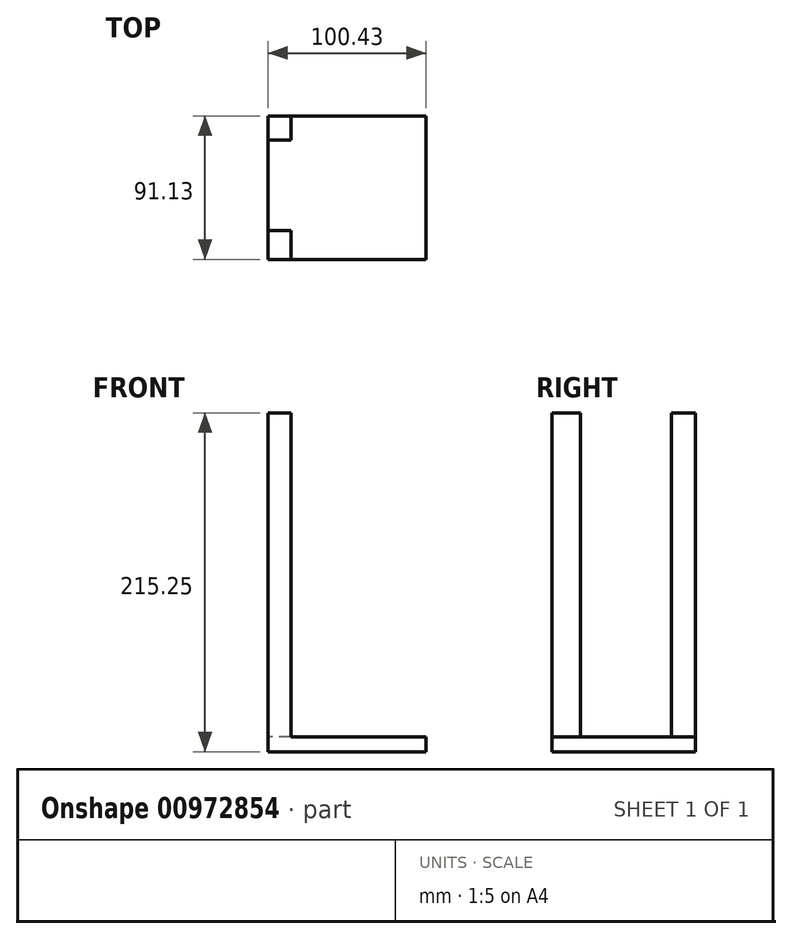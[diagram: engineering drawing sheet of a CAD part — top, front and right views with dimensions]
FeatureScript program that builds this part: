
annotation { "Feature Type Name" : "Feature", "Feature Type Description" : "" }
export const myFeature = defineFeature(function(context is Context, id is Id, definition is map)
    precondition{}
    {
        {
            var Q0;
            Q0=qCreatedBy(makeId("Top.planeOp"),FACE);
            var sketch = newSketch(context, id + "F0", { "sketchPlane" : qUnion([Q0])});
            skLineSegment(sketch, "E0.bottom", {"start": v(-43.08, 37.12) * mm, "end": v(57.35, 37.12) * mm});
            skLineSegment(sketch, "E0.top", {"start": v(-43.08, -54.01) * mm, "end": v(57.35, -54.01) * mm});
            skLineSegment(sketch, "E0.left", {"start": v(-43.08, 37.12) * mm, "end": v(-43.08, -54.01) * mm});
            skLineSegment(sketch, "E0.right", {"start": v(57.35, 37.12) * mm, "end": v(57.35, -54.01) * mm});
            skLineSegment(sketch, "E1", {"start": v(-29.36, 37.12) * mm, "end": v(-29.36, -54.01) * mm});
            skLineSegment(sketch, "E2", {"start": v(40.88, 37.12) * mm, "end": v(40.88, -54.01) * mm});
            skLineSegment(sketch, "E3", {"start": v(-43.08, 23.98) * mm, "end": v(57.35, 23.98) * mm});
            skLineSegment(sketch, "E4", {"start": v(-43.08, -38.08) * mm, "end": v(57.35, -38.08) * mm});
            skSolve(sketch);
        }
        {
            var Q0;
            {var subQ0=sQuery(id+"F0.wireOp",EDGE,"E0.right");var subQ1=sQuery(id+"F0.wireOp",EDGE,"E0.bottom");var subQ2=makeQuery(id+"F0.imprint","INTERSECT",VERTEX,{"derivedFrom":[subQ1,subQ0]});Q0=makeQuery(id+"F0.imprint","IMPRINT",FACE,{"disambiguationData":[TD([[makeQuery(id+"F0.imprint","IMPRINT",EDGE,{"disambiguationData":[TD([[subQ2,1.0]])],"derivedFrom":subQ1}),-1.0]])]});}
            var Q1;
            {var subQ0=sQuery(id+"F0.wireOp",EDGE,"E3");var subQ1=sQuery(id+"F0.wireOp",EDGE,"E0.right");var subQ2=makeQuery(id+"F0.imprint","INTERSECT",VERTEX,{"derivedFrom":[subQ1,subQ0]});Q1=makeQuery(id+"F0.imprint","IMPRINT",FACE,{"disambiguationData":[TD([[makeQuery(id+"F0.imprint","IMPRINT",EDGE,{"disambiguationData":[TD([[subQ2,-1.0]])],"derivedFrom":subQ1}),-1.0]])]});}
            var Q2;
            Q2 = qSketchRegion(id + "F0", true);
            var Q3;
            {var subQ0=sQuery(id+"F0.wireOp",EDGE,"E1");var subQ1=sQuery(id+"F0.wireOp",EDGE,"E0.top");var subQ2=makeQuery(id+"F0.imprint","INTERSECT",VERTEX,{"derivedFrom":[subQ1,subQ0]});Q3=makeQuery(id+"F0.imprint","IMPRINT",FACE,{"disambiguationData":[TD([[makeQuery(id+"F0.imprint","IMPRINT",EDGE,{"disambiguationData":[TD([[subQ2,-1.0]])],"derivedFrom":subQ1}),1.0]])]});}
            var Q4;
            {var subQ0=sQuery(id+"F0.wireOp",EDGE,"E1");var subQ1=sQuery(id+"F0.wireOp",EDGE,"E0.bottom");var subQ2=makeQuery(id+"F0.imprint","INTERSECT",VERTEX,{"derivedFrom":[subQ1,subQ0]});Q4=makeQuery(id+"F0.imprint","IMPRINT",FACE,{"disambiguationData":[TD([[makeQuery(id+"F0.imprint","IMPRINT",EDGE,{"disambiguationData":[TD([[subQ2,-1.0]])],"derivedFrom":subQ1}),-1.0]])]});}
            var Q5;
            {var subQ0=sQuery(id+"F0.wireOp",EDGE,"E0.right");var subQ1=sQuery(id+"F0.wireOp",EDGE,"E0.top");var subQ2=makeQuery(id+"F0.imprint","INTERSECT",VERTEX,{"derivedFrom":[subQ1,subQ0]});Q5=makeQuery(id+"F0.imprint","IMPRINT",FACE,{"disambiguationData":[TD([[makeQuery(id+"F0.imprint","IMPRINT",EDGE,{"disambiguationData":[TD([[subQ2,1.0]])],"derivedFrom":subQ1}),1.0]])]});}
            var Q6;
            {var subQ0=sQuery(id+"F0.wireOp",EDGE,"E3");var subQ1=sQuery(id+"F0.wireOp",EDGE,"E0.left");var subQ2=makeQuery(id+"F0.imprint","INTERSECT",VERTEX,{"derivedFrom":[subQ1,subQ0]});Q6=makeQuery(id+"F0.imprint","IMPRINT",FACE,{"disambiguationData":[TD([[makeQuery(id+"F0.imprint","IMPRINT",EDGE,{"disambiguationData":[TD([[subQ2,-1.0]])],"derivedFrom":subQ1}),1.0]])]});}
            var Q7;
            {var subQ0=sQuery(id+"F0.wireOp",EDGE,"E0.left");var subQ1=sQuery(id+"F0.wireOp",EDGE,"E0.top");var subQ2=makeQuery(id+"F0.imprint","INTERSECT",VERTEX,{"derivedFrom":[subQ1,subQ0]});Q7=makeQuery(id+"F0.imprint","IMPRINT",FACE,{"disambiguationData":[TD([[makeQuery(id+"F0.imprint","IMPRINT",EDGE,{"disambiguationData":[TD([[subQ2,-1.0]])],"derivedFrom":subQ1}),1.0]])]});}
            var Q8;
            {var subQ0=sQuery(id+"F0.wireOp",EDGE,"E0.left");var subQ1=sQuery(id+"F0.wireOp",EDGE,"E0.bottom");var subQ2=makeQuery(id+"F0.imprint","INTERSECT",VERTEX,{"derivedFrom":[subQ1,subQ0]});Q8=makeQuery(id+"F0.imprint","IMPRINT",FACE,{"disambiguationData":[TD([[makeQuery(id+"F0.imprint","IMPRINT",EDGE,{"disambiguationData":[TD([[subQ2,-1.0]])],"derivedFrom":subQ1}),-1.0]])]});}
            var Q9;
            {var subQ0=sQuery(id+"F0.wireOp",EDGE,"E3");var subQ1=sQuery(id+"F0.wireOp",EDGE,"E1");var subQ2=makeQuery(id+"F0.imprint","INTERSECT",VERTEX,{"derivedFrom":[subQ1,subQ0]});Q9=makeQuery(id+"F0.imprint","IMPRINT",FACE,{"disambiguationData":[TD([[makeQuery(id+"F0.imprint","IMPRINT",EDGE,{"disambiguationData":[TD([[subQ2,-1.0]])],"derivedFrom":subQ1}),1.0]])]});}
            extrude(context, id + "F1", {"entities" : qUnion([Q0, Q1, Q2, Q3, Q4, Q5, Q6, Q7, Q8, Q9]), "depth" : 9.53 * mm, "offsetDistance" : 25.4 * mm});
        }
        {
            var Q0;
            Q0=makeQuery(id+"F1.opExtrude","CAP_FACE",FACE,{"disambiguationData":[OSD([sQuery(id+"F0.wireOp",EDGE,"E0.bottom"),sQuery(id+"F0.wireOp",EDGE,"E0.top"),sQuery(id+"F0.wireOp",EDGE,"E0.left"),sQuery(id+"F0.wireOp",EDGE,"E0.right")])],"isStart":false});
            var sketch = newSketch(context, id + "F2", { "sketchPlane" : qUnion([Q0])});
            skLineSegment(sketch, "E5", {"start": v(-28.54, 37.12) * mm, "end": v(-28.54, -54.01) * mm});
            skLineSegment(sketch, "E6", {"start": v(40.88, 37.12) * mm, "end": v(40.88, -54.01) * mm});
            skLineSegment(sketch, "E7", {"start": v(57.35, 21.79) * mm, "end": v(-43.08, 21.79) * mm});
            skLineSegment(sketch, "E8", {"start": v(57.35, -35.89) * mm, "end": v(-43.08, -35.89) * mm});
            skSolve(sketch);
        }
        {
            var Q0;
            {var subQ0=sQuery(id+"F2.wireOp",EDGE,"E5");var subQ1=makeQuery(id+"F1.opExtrude","CAP_EDGE",EDGE,{"disambiguationData":[OSD([sQuery(id+"F0.wireOp",EDGE,"E0.bottom")])],"isStart":false});var subQ2=makeQuery(id+"F2.imprint","INTERSECT",VERTEX,{"derivedFrom":[subQ1,subQ0]});Q0=makeQuery(id+"F2.imprint","IMPRINT",FACE,{"disambiguationData":[TD([[makeQuery(id+"F2.imprint","IMPRINT",EDGE,{"disambiguationData":[TD([[subQ2,-1.0]])],"derivedFrom":subQ0}),-1.0]])]});}
            var Q1;
            {var subQ0=sQuery(id+"F2.wireOp",EDGE,"E5");var subQ1=makeQuery(id+"F1.opExtrude","CAP_EDGE",EDGE,{"disambiguationData":[OSD([sQuery(id+"F0.wireOp",EDGE,"E0.top")])],"isStart":false});var subQ2=makeQuery(id+"F2.imprint","INTERSECT",VERTEX,{"derivedFrom":[subQ1,subQ0]});Q1=makeQuery(id+"F2.imprint","IMPRINT",FACE,{"disambiguationData":[TD([[makeQuery(id+"F2.imprint","IMPRINT",EDGE,{"disambiguationData":[TD([[subQ2,1.0]])],"derivedFrom":subQ0}),-1.0]])]});}
            extrude(context, id + "F3", {"entities" : qUnion([Q0, Q1]), "operationType" : NewBodyOperationType.ADD, "depth" : 205.72 * mm, "offsetDistance" : 25.4 * mm});
        }
        {
            var Q0;
            Q0=makeQuery(id+"F3.opExtrude","SWEPT_FACE",FACE,{"disambiguationData":[OSD([sQuery(id+"F2.wireOp",EDGE,"E8")])]});
            var sketch = newSketch(context, id + "F4", { "sketchPlane" : qUnion([Q0])});
            skLineSegment(sketch, "E9", {"start": v(43.08, 206) * mm, "end": v(28.54, 206) * mm});
            skSolve(sketch);
        }
        {
            var Q0;
            Q0=sQuery(id+"F4.wireOp",EDGE,"E9");
            var Q1;
            Q1=makeQuery(id+"F3.opExtrude","SWEPT_FACE",FACE,{"disambiguationData":[OSD([sQuery(id+"F2.wireOp",EDGE,"E7")])]});
            extrude(context, id + "F5", {"bodyType" : ToolBodyType.SURFACE, "surfaceEntities" : qUnion([Q0]), "endBound" : BoundingType.UP_TO_SURFACE, "depth" : 25.4 * mm, "endBoundEntityFace" : qUnion([Q1]), "offsetDistance" : 25.4 * mm});
        }
    });
